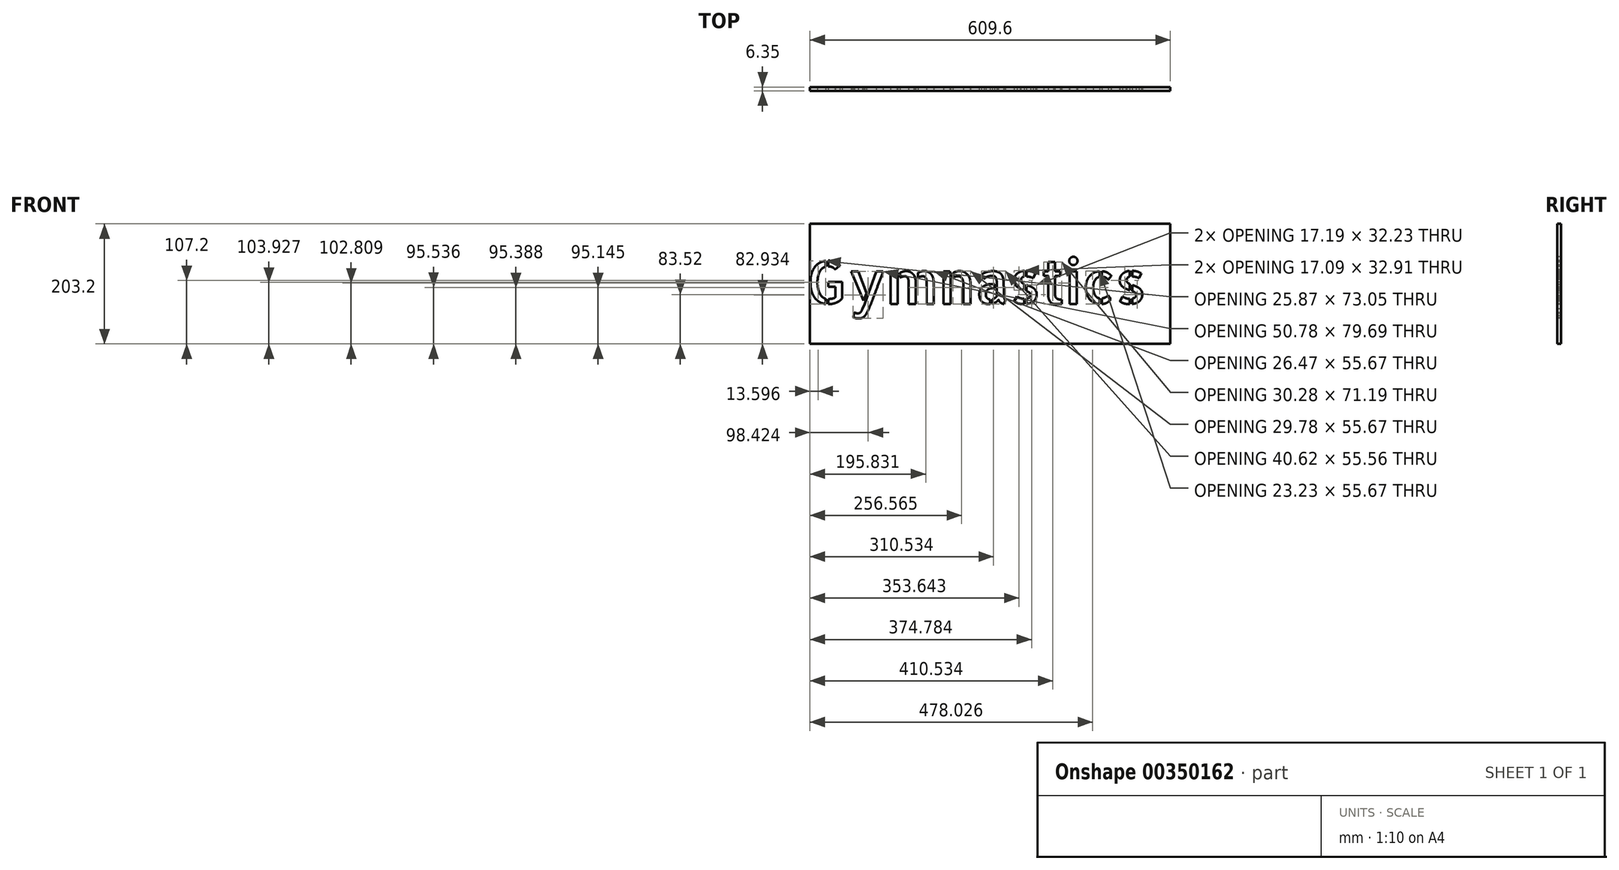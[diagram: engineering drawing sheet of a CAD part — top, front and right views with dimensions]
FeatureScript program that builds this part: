
annotation { "Feature Type Name" : "Feature", "Feature Type Description" : "" }
export const myFeature = defineFeature(function(context is Context, id is Id, definition is map)
    precondition{}
    {
        {
            var Q0;
            Q0=qCreatedBy(makeId("Front.planeOp"),FACE);
            var sketch = newSketch(context, id + "F0", { "sketchPlane" : qUnion([Q0])});
            skLineSegment(sketch, "E0.bottom", {"start": v(0, 0) * mm, "end": v(609.6, 0) * mm});
            skLineSegment(sketch, "E0.top", {"start": v(0, 203.2) * mm, "end": v(609.6, 203.2) * mm});
            skLineSegment(sketch, "E0.left", {"start": v(0, 0) * mm, "end": v(0, 203.2) * mm});
            skLineSegment(sketch, "E0.right", {"start": v(609.6, 0) * mm, "end": v(609.6, 203.2) * mm});
            skSolve(sketch);
        }
        {
            var Q0;
            Q0 = qSketchRegion(id + "F0", true);
            extrude(context, id + "F1", {"entities" : qUnion([Q0]), "depth" : 6.35 * mm});
        }
        {
            var Q0;
            Q0=makeQuery(id+"F1.opExtrude","CAP_FACE",FACE,{"disambiguationData":[OSD([sQuery(id+"F0.wireOp",EDGE,"E0.bottom"),sQuery(id+"F0.wireOp",EDGE,"E0.top"),sQuery(id+"F0.wireOp",EDGE,"E0.left"),sQuery(id+"F0.wireOp",EDGE,"E0.right")])],"isStart":false});
            var sketch = newSketch(context, id + "F2", { "sketchPlane" : qUnion([Q0])});
            skText(sketch, "E1", { "text": "Gymnastics", "fontName": "AllertaStencil-Regular.ttf"});
            skPoint(sketch, "E2", {"position": v(304.8, 203.2) * mm});
            const initialGuessF2  = {"E1": [-0.00706, 0.0677, 1, 0, 0.072]};
            skSetInitialGuess(sketch, initialGuessF2);
            skSolve(sketch);
        }
        {
            var Q0;
            Q0 = qSketchRegion(id + "F2", true);
            extrude(context, id + "F3", {"entities" : qUnion([Q0]), "operationType" : NewBodyOperationType.REMOVE, "endBound" : BoundingType.THROUGH_ALL, "oppositeDirection" : true, "depth" : 25.4 * mm});
        }
    });
